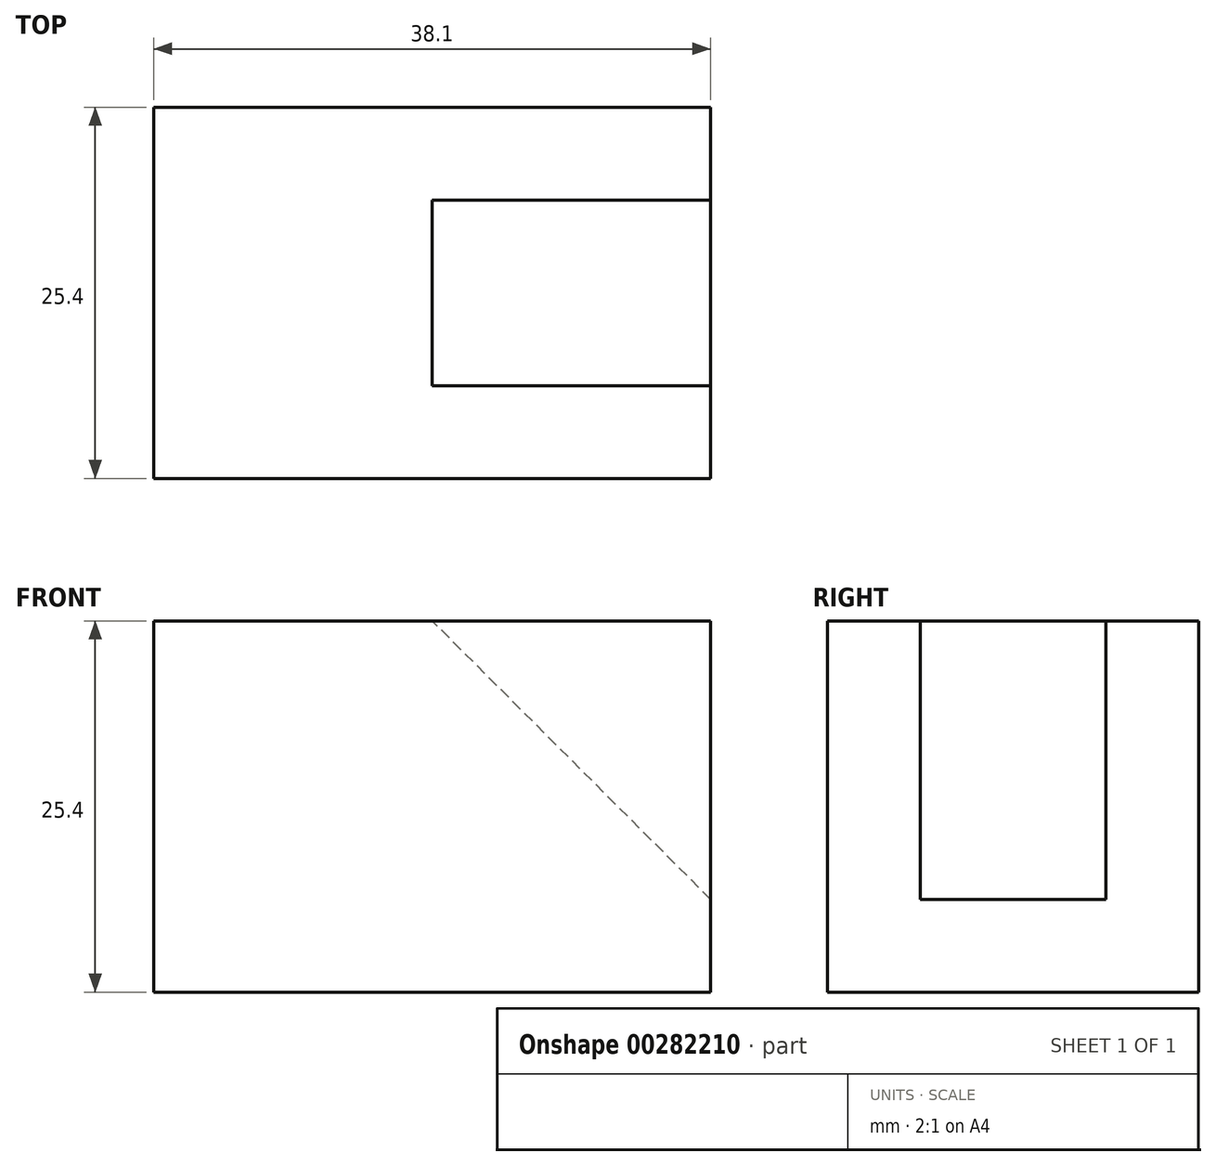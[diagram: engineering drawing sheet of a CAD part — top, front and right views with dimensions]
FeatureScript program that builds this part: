
annotation { "Feature Type Name" : "Feature", "Feature Type Description" : "" }
export const myFeature = defineFeature(function(context is Context, id is Id, definition is map)
    precondition{}
    {
        {
            var Q0;
            Q0=qCreatedBy(makeId("Front.planeOp"),FACE);
            var sketch = newSketch(context, id + "F0", { "sketchPlane" : qUnion([Q0])});
            skLineSegment(sketch, "E0", {"start": v(0, 0) * mm, "end": v(0, -25.4) * mm});
            skLineSegment(sketch, "E1", {"start": v(0, -25.4) * mm, "end": v(38.1, -25.4) * mm});
            skLineSegment(sketch, "E2", {"start": v(38.1, -25.4) * mm, "end": v(38.1, 0) * mm});
            skLineSegment(sketch, "E3", {"start": v(38.1, 0) * mm, "end": v(0, 0) * mm});
            skSolve(sketch);
        }
        {
            var Q0;
            Q0=makeQuery(id+"F0.imprint","IMPRINT",FACE,{"disambiguationData":[TD([[makeQuery(id+"F0.imprint","IMPRINT",EDGE,{"derivedFrom":sQuery(id+"F0.wireOp",EDGE,"E0")}),1.0]])]});
            extrude(context, id + "F1", {"entities" : qUnion([Q0]), "endBound" : BoundingType.SYMMETRIC, "depth" : 25.4 * mm});
        }
        {
            var Q0;
            Q0=qCreatedBy(makeId("Front.planeOp"),FACE);
            var sketch = newSketch(context, id + "F2", { "sketchPlane" : qUnion([Q0])});
            skLineSegment(sketch, "E4", {"start": v(19.05, 0) * mm, "end": v(38.1, 0) * mm});
            skLineSegment(sketch, "E5", {"start": v(38.1, 0) * mm, "end": v(38.1, -19.05) * mm});
            skLineSegment(sketch, "E6", {"start": v(38.1, -19.05) * mm, "end": v(19.05, 0) * mm});
            skSolve(sketch);
        }
        {
            var Q0;
            Q0 = qSketchRegion(id + "F2", true);
            extrude(context, id + "F3", {"entities" : qUnion([Q0]), "operationType" : NewBodyOperationType.REMOVE, "endBound" : BoundingType.SYMMETRIC, "depth" : 12.7 * mm});
        }
    });
